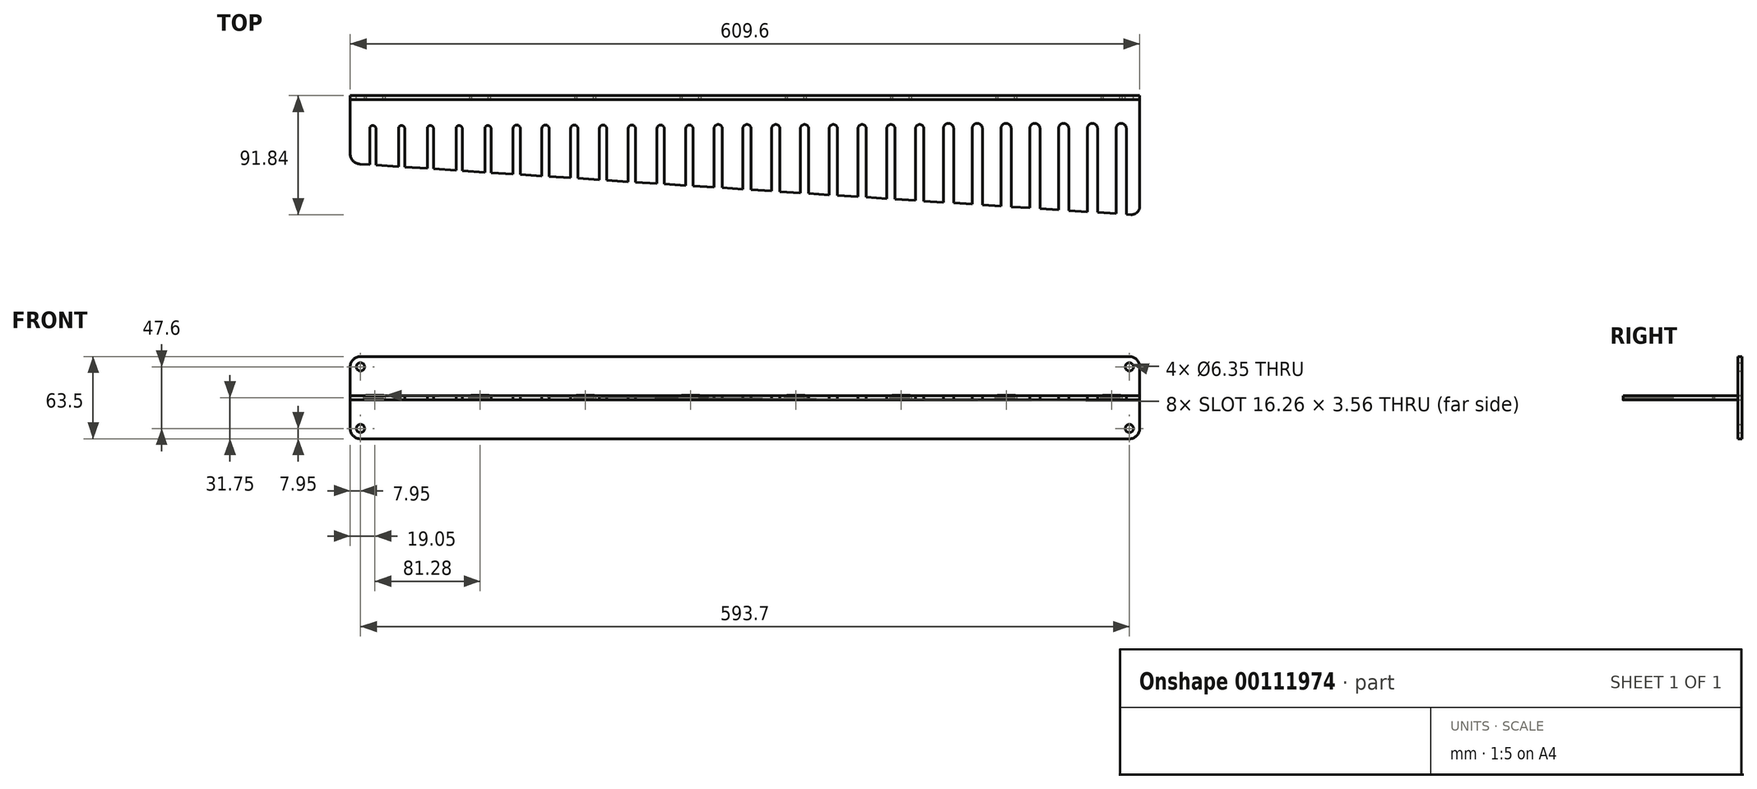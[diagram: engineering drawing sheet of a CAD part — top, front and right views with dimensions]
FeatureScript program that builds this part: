
annotation { "Feature Type Name" : "Feature", "Feature Type Description" : "" }
export const myFeature = defineFeature(function(context is Context, id is Id, definition is map)
    precondition{}
    {
        {
            var Q0;
            Q0=qCreatedBy(makeId("Front.planeOp"),FACE);
            var sketch = newSketch(context, id + "F0", { "sketchPlane" : qUnion([Q0])});
            skLineSegment(sketch, "E0.bottom", {"start": v(-296.85, -31.75) * mm, "end": v(296.85, -31.75) * mm});
            skLineSegment(sketch, "E0.top", {"start": v(-296.85, 31.75) * mm, "end": v(296.85, 31.75) * mm});
            skLineSegment(sketch, "E0.left", {"start": v(-304.8, -23.8) * mm, "end": v(-304.8, 23.8) * mm});
            skLineSegment(sketch, "E0.right", {"start": v(304.8, -23.8) * mm, "end": v(304.8, 23.8) * mm});
            skPoint(sketch, "E0.middle", {"position": v(0, 0) * mm});
            skPoint(sketch, "E1.visualSharp", {"position": v(304.8, 31.75) * mm});
            skArc(sketch, "E1.filletArc", {"start": v(304.8, 23.8) * mm, "mid": v(302.47, 29.42) * mm, "end": v(296.85, 31.75) * mm});
            skPoint(sketch, "E2.visualSharp", {"position": v(304.8, -31.75) * mm});
            skArc(sketch, "E2.filletArc", {"start": v(296.85, -31.75) * mm, "mid": v(302.47, -29.42) * mm, "end": v(304.8, -23.8) * mm});
            skPoint(sketch, "E3.visualSharp", {"position": v(-304.8, -31.75) * mm});
            skArc(sketch, "E3.filletArc", {"start": v(-304.8, -23.8) * mm, "mid": v(-302.47, -29.42) * mm, "end": v(-296.85, -31.75) * mm});
            skPoint(sketch, "E4.visualSharp", {"position": v(-304.8, 31.75) * mm});
            skArc(sketch, "E4.filletArc", {"start": v(-296.85, 31.75) * mm, "mid": v(-302.47, 29.42) * mm, "end": v(-304.8, 23.8) * mm});
            skPoint(sketch, "E5", {"position": v(-304.8, 0) * mm});
            skLineSegment(sketch, "E6", {"start": v(-292.1, 0) * mm, "end": v(-279.4, 0) * mm});
            skArc(sketch, "E7.0.startCap", {"start": v(-292.1, -1.78) * mm, "mid": v(-293.88, 0) * mm, "end": v(-292.1, 1.78) * mm});
            skArc(sketch, "E7.0.endCap", {"start": v(-279.4, 1.78) * mm, "mid": v(-277.62, 0) * mm, "end": v(-279.4, -1.78) * mm});
            skLineSegment(sketch, "E7.0.left", {"start": v(-292.1, 1.78) * mm, "end": v(-279.4, 1.78) * mm});
            skLineSegment(sketch, "E7.0.right", {"start": v(-292.1, -1.78) * mm, "end": v(-279.4, -1.78) * mm});
            skLineSegment(sketch, "E8.1.0.0", {"start": v(-210.82, -1.78) * mm, "end": v(-198.12, -1.78) * mm});
            skLineSegment(sketch, "E8.1.0.1", {"start": v(-210.82, 1.78) * mm, "end": v(-198.12, 1.78) * mm});
            skArc(sketch, "E8.1.0.2", {"start": v(-198.12, 1.78) * mm, "mid": v(-196.34, 0) * mm, "end": v(-198.12, -1.78) * mm});
            skArc(sketch, "E8.1.0.3", {"start": v(-210.82, -1.78) * mm, "mid": v(-212.6, 0) * mm, "end": v(-210.82, 1.78) * mm});
            skLineSegment(sketch, "E8.1.0.4", {"start": v(-210.82, 0) * mm, "end": v(-198.12, 0) * mm});
            skLineSegment(sketch, "E8.2.0.0", {"start": v(-129.54, -1.78) * mm, "end": v(-116.84, -1.78) * mm});
            skLineSegment(sketch, "E8.2.0.1", {"start": v(-129.54, 1.78) * mm, "end": v(-116.84, 1.78) * mm});
            skArc(sketch, "E8.2.0.2", {"start": v(-116.84, 1.78) * mm, "mid": v(-115.06, 0) * mm, "end": v(-116.84, -1.78) * mm});
            skArc(sketch, "E8.2.0.3", {"start": v(-129.54, -1.78) * mm, "mid": v(-131.32, 0) * mm, "end": v(-129.54, 1.78) * mm});
            skLineSegment(sketch, "E8.2.0.4", {"start": v(-129.54, 0) * mm, "end": v(-116.84, 0) * mm});
            skLineSegment(sketch, "E8.3.0.0", {"start": v(-48.26, -1.78) * mm, "end": v(-35.56, -1.78) * mm});
            skLineSegment(sketch, "E8.3.0.1", {"start": v(-48.26, 1.78) * mm, "end": v(-35.56, 1.78) * mm});
            skArc(sketch, "E8.3.0.2", {"start": v(-35.56, 1.78) * mm, "mid": v(-33.78, 0) * mm, "end": v(-35.56, -1.78) * mm});
            skArc(sketch, "E8.3.0.3", {"start": v(-48.26, -1.78) * mm, "mid": v(-50.04, 0) * mm, "end": v(-48.26, 1.78) * mm});
            skLineSegment(sketch, "E8.3.0.4", {"start": v(-48.26, 0) * mm, "end": v(-35.56, 0) * mm});
            skLineSegment(sketch, "E8.4.0.0", {"start": v(33.02, -1.78) * mm, "end": v(45.72, -1.78) * mm});
            skLineSegment(sketch, "E8.4.0.1", {"start": v(33.02, 1.78) * mm, "end": v(45.72, 1.78) * mm});
            skArc(sketch, "E8.4.0.2", {"start": v(45.72, 1.78) * mm, "mid": v(47.5, 0) * mm, "end": v(45.72, -1.78) * mm});
            skArc(sketch, "E8.4.0.3", {"start": v(33.02, -1.78) * mm, "mid": v(31.24, 0) * mm, "end": v(33.02, 1.78) * mm});
            skLineSegment(sketch, "E8.4.0.4", {"start": v(33.02, 0) * mm, "end": v(45.72, 0) * mm});
            skLineSegment(sketch, "E8.5.0.0", {"start": v(114.3, -1.78) * mm, "end": v(127, -1.78) * mm});
            skLineSegment(sketch, "E8.5.0.1", {"start": v(114.3, 1.78) * mm, "end": v(127, 1.78) * mm});
            skArc(sketch, "E8.5.0.2", {"start": v(127, 1.78) * mm, "mid": v(128.78, 0) * mm, "end": v(127, -1.78) * mm});
            skArc(sketch, "E8.5.0.3", {"start": v(114.3, -1.78) * mm, "mid": v(112.52, 0) * mm, "end": v(114.3, 1.78) * mm});
            skLineSegment(sketch, "E8.5.0.4", {"start": v(114.3, 0) * mm, "end": v(127, 0) * mm});
            skLineSegment(sketch, "E8.6.0.0", {"start": v(195.58, -1.78) * mm, "end": v(208.28, -1.78) * mm});
            skLineSegment(sketch, "E8.6.0.1", {"start": v(195.58, 1.78) * mm, "end": v(208.28, 1.78) * mm});
            skArc(sketch, "E8.6.0.2", {"start": v(208.28, 1.78) * mm, "mid": v(210.06, 0) * mm, "end": v(208.28, -1.78) * mm});
            skArc(sketch, "E8.6.0.3", {"start": v(195.58, -1.78) * mm, "mid": v(193.8, 0) * mm, "end": v(195.58, 1.78) * mm});
            skLineSegment(sketch, "E8.6.0.4", {"start": v(195.58, 0) * mm, "end": v(208.28, 0) * mm});
            skLineSegment(sketch, "E8.7.0.0", {"start": v(276.86, -1.78) * mm, "end": v(289.56, -1.78) * mm});
            skLineSegment(sketch, "E8.7.0.1", {"start": v(276.86, 1.78) * mm, "end": v(289.56, 1.78) * mm});
            skArc(sketch, "E8.7.0.2", {"start": v(289.56, 1.78) * mm, "mid": v(291.34, 0) * mm, "end": v(289.56, -1.78) * mm});
            skArc(sketch, "E8.7.0.3", {"start": v(276.86, -1.78) * mm, "mid": v(275.08, 0) * mm, "end": v(276.86, 1.78) * mm});
            skLineSegment(sketch, "E8.7.0.4", {"start": v(276.86, 0) * mm, "end": v(289.56, 0) * mm});
            skLineSegment(sketch, "E8.direction1", {"start": v(-292.1, -1.78) * mm, "end": v(-210.82, -1.78) * mm, "construction": true});
            skCircle(sketch, "E9", {"center": v(-296.85, 23.8) * mm, "radius": 3.18 * mm});
            skCircle(sketch, "E10", {"center": v(-296.85, -23.8) * mm, "radius": 3.18 * mm});
            skCircle(sketch, "E11", {"center": v(296.85, -23.8) * mm, "radius": 3.18 * mm});
            skCircle(sketch, "E12", {"center": v(296.85, 23.8) * mm, "radius": 3.18 * mm});
            skSolve(sketch);
        }
        {
            var Q0;
            Q0 = qSketchRegion(id + "F0", true);
            extrude(context, id + "F1", {"entities" : qUnion([Q0]), "offsetDistance" : 25.4 * mm, "depth" : 3.17 * mm});
        }
        {
            var Q0;
            Q0=makeQuery(id+"F1.opExtrude","SWEPT_FACE",FACE,{"disambiguationData":[OSD([sQuery(id+"F0.wireOp",EDGE,"E7.0.right")])]});
            var sketch = newSketch(context, id + "F2", { "sketchPlane" : qUnion([Q0])});
            skLineSegment(sketch, "E13", {"start": v(289.56, -3.18) * mm, "end": v(304.8, -3.18) * mm});
            skLineSegment(sketch, "E14", {"start": v(208.28, -3.18) * mm, "end": v(276.86, -3.18) * mm});
            skLineSegment(sketch, "E15", {"start": v(127, -3.18) * mm, "end": v(195.58, -3.18) * mm});
            skLineSegment(sketch, "E16", {"start": v(45.72, -3.18) * mm, "end": v(114.3, -3.18) * mm});
            skLineSegment(sketch, "E17", {"start": v(-35.56, -3.18) * mm, "end": v(33.02, -3.18) * mm});
            skLineSegment(sketch, "E18", {"start": v(-116.84, -3.18) * mm, "end": v(-48.26, -3.18) * mm});
            skLineSegment(sketch, "E19", {"start": v(-198.12, -3.18) * mm, "end": v(-129.54, -3.18) * mm});
            skLineSegment(sketch, "E20", {"start": v(-279.4, -3.18) * mm, "end": v(-210.82, -3.18) * mm});
            skLineSegment(sketch, "E21", {"start": v(-304.8, -3.18) * mm, "end": v(-292.1, -3.18) * mm});
            skLineSegment(sketch, "E22", {"start": v(-292.1, 0) * mm, "end": v(-279.4, 0) * mm});
            skLineSegment(sketch, "E23", {"start": v(-292.1, -3.18) * mm, "end": v(-292.1, 0) * mm});
            skLineSegment(sketch, "E24", {"start": v(-279.4, -3.18) * mm, "end": v(-279.4, 0) * mm});
            skLineSegment(sketch, "E25", {"start": v(-210.82, 0) * mm, "end": v(-198.12, 0) * mm});
            skLineSegment(sketch, "E26", {"start": v(-210.82, -3.18) * mm, "end": v(-210.82, 0) * mm});
            skLineSegment(sketch, "E27", {"start": v(-198.12, -3.18) * mm, "end": v(-198.12, 0) * mm});
            skLineSegment(sketch, "E28", {"start": v(-129.54, 0) * mm, "end": v(-116.84, 0) * mm});
            skLineSegment(sketch, "E29", {"start": v(-129.54, -3.18) * mm, "end": v(-129.54, 0) * mm});
            skLineSegment(sketch, "E30", {"start": v(-116.84, -3.18) * mm, "end": v(-116.84, 0) * mm});
            skLineSegment(sketch, "E31", {"start": v(-48.26, 0) * mm, "end": v(-35.56, 0) * mm});
            skLineSegment(sketch, "E32", {"start": v(-48.26, -3.18) * mm, "end": v(-48.26, 0) * mm});
            skLineSegment(sketch, "E33", {"start": v(-35.56, -3.18) * mm, "end": v(-35.56, 0) * mm});
            skLineSegment(sketch, "E34", {"start": v(33.02, 0) * mm, "end": v(45.72, 0) * mm});
            skLineSegment(sketch, "E35", {"start": v(33.02, -3.18) * mm, "end": v(33.02, 0) * mm});
            skLineSegment(sketch, "E36", {"start": v(45.72, -3.18) * mm, "end": v(45.72, 0) * mm});
            skLineSegment(sketch, "E37", {"start": v(114.3, 0) * mm, "end": v(127, 0) * mm});
            skLineSegment(sketch, "E38", {"start": v(114.3, -3.18) * mm, "end": v(114.3, 0) * mm});
            skLineSegment(sketch, "E39", {"start": v(127, -3.18) * mm, "end": v(127, 0) * mm});
            skLineSegment(sketch, "E40", {"start": v(195.58, 0) * mm, "end": v(208.28, 0) * mm});
            skLineSegment(sketch, "E41", {"start": v(195.58, -3.18) * mm, "end": v(195.58, 0) * mm});
            skLineSegment(sketch, "E42", {"start": v(208.28, -3.18) * mm, "end": v(208.28, 0) * mm});
            skLineSegment(sketch, "E43", {"start": v(276.86, 0) * mm, "end": v(289.56, 0) * mm});
            skLineSegment(sketch, "E44", {"start": v(276.86, -3.18) * mm, "end": v(276.86, 0) * mm});
            skLineSegment(sketch, "E45", {"start": v(289.56, -3.18) * mm, "end": v(289.56, 0) * mm});
            skPoint(sketch, "E46.end.orphan", {"position": v(-279.4, -3.18) * mm});
            skPoint(sketch, "E46.start.orphan", {"position": v(-292.1, -3.18) * mm});
            skPoint(sketch, "E47.end.orphan", {"position": v(-198.12, -3.18) * mm});
            skPoint(sketch, "E47.start.orphan", {"position": v(-210.82, -3.18) * mm});
            skPoint(sketch, "E48.end.orphan", {"position": v(-116.84, -3.18) * mm});
            skPoint(sketch, "E48.start.orphan", {"position": v(-129.54, -3.18) * mm});
            skPoint(sketch, "E49.end.orphan", {"position": v(45.72, -3.18) * mm});
            skPoint(sketch, "E49.start.orphan", {"position": v(33.02, -3.18) * mm});
            skPoint(sketch, "E50.end.orphan", {"position": v(127, -3.18) * mm});
            skPoint(sketch, "E50.start.orphan", {"position": v(114.3, -3.18) * mm});
            skPoint(sketch, "E51.end.orphan", {"position": v(-35.56, -3.18) * mm});
            skPoint(sketch, "E51.start.orphan", {"position": v(-48.26, -3.18) * mm});
            skPoint(sketch, "E52.end.orphan", {"position": v(208.28, -3.18) * mm});
            skPoint(sketch, "E52.start.orphan", {"position": v(195.58, -3.18) * mm});
            skPoint(sketch, "E53.end.orphan", {"position": v(289.56, -3.18) * mm});
            skPoint(sketch, "E53.start.orphan", {"position": v(276.86, -3.18) * mm});
            skLineSegment(sketch, "E54", {"start": v(-297.37, -52.8) * mm, "end": v(298.03, -91.82) * mm});
            skLineSegment(sketch, "E55", {"start": v(304.8, -85.49) * mm, "end": v(304.8, -3.17) * mm});
            skPoint(sketch, "E56.visualSharp", {"position": v(304.8, -92.27) * mm});
            skArc(sketch, "E56.filletArc", {"start": v(298.03, -91.82) * mm, "mid": v(302.8, -90.12) * mm, "end": v(304.8, -85.49) * mm});
            skLineSegment(sketch, "E57", {"start": v(-304.8, -3.18) * mm, "end": v(-304.8, -44.87) * mm});
            skPoint(sketch, "E58.visualSharp", {"position": v(-304.8, -52.31) * mm});
            skArc(sketch, "E58.filletArc", {"start": v(-304.8, -44.87) * mm, "mid": v(-302.65, -50.3) * mm, "end": v(-297.37, -52.8) * mm});
            skLineSegment(sketch, "E59", {"start": v(290.51, -91.33) * mm, "end": v(290.51, -25.4) * mm});
            skLineSegment(sketch, "E60.1.0.0", {"start": v(268.29, -91.33) * mm, "end": v(268.29, -25.4) * mm});
            skLineSegment(sketch, "E60.2.0.0", {"start": v(246.06, -91.33) * mm, "end": v(246.06, -25.4) * mm});
            skLineSegment(sketch, "E60.direction1", {"start": v(290.51, -91.33) * mm, "end": v(268.29, -91.33) * mm, "construction": true});
            skLineSegment(sketch, "E61.0.3.0", {"start": v(223.84, -91.33) * mm, "end": v(223.84, -25.4) * mm});
            skLineSegment(sketch, "E61.0.4.0", {"start": v(201.61, -91.33) * mm, "end": v(201.61, -25.4) * mm});
            skLineSegment(sketch, "E61.0.5.0", {"start": v(179.39, -91.33) * mm, "end": v(179.39, -25.4) * mm});
            skLineSegment(sketch, "E62.0.6.0", {"start": v(157.16, -91.33) * mm, "end": v(157.16, -25.4) * mm});
            skLineSegment(sketch, "E63.0.7.0", {"start": v(134.94, -91.33) * mm, "end": v(134.94, -25.4) * mm});
            skLineSegment(sketch, "E64.0.8.0", {"start": v(112.71, -91.33) * mm, "end": v(112.71, -25.4) * mm});
            skLineSegment(sketch, "E65.0.9.0", {"start": v(90.49, -91.33) * mm, "end": v(90.49, -25.4) * mm});
            skLineSegment(sketch, "E66.0.10.0", {"start": v(68.26, -91.33) * mm, "end": v(68.26, -25.4) * mm});
            skLineSegment(sketch, "E67.0.11.0", {"start": v(46.04, -91.33) * mm, "end": v(46.04, -25.4) * mm});
            skLineSegment(sketch, "E68.0.12.0", {"start": v(23.81, -91.33) * mm, "end": v(23.81, -25.4) * mm});
            skLineSegment(sketch, "E69.0.13.0", {"start": v(1.59, -91.33) * mm, "end": v(1.59, -25.4) * mm});
            skLineSegment(sketch, "E70.0.14.0", {"start": v(-20.64, -91.33) * mm, "end": v(-20.64, -25.4) * mm});
            skLineSegment(sketch, "E71.0.15.0", {"start": v(-42.86, -91.33) * mm, "end": v(-42.86, -25.4) * mm});
            skLineSegment(sketch, "E72.0.16.0", {"start": v(-65.09, -91.33) * mm, "end": v(-65.09, -25.4) * mm});
            skLineSegment(sketch, "E73.0.17.0", {"start": v(-87.31, -91.33) * mm, "end": v(-87.31, -25.4) * mm});
            skLineSegment(sketch, "E74.0.18.0", {"start": v(-109.54, -91.33) * mm, "end": v(-109.54, -25.4) * mm});
            skLineSegment(sketch, "E75.0.19.0", {"start": v(-131.76, -91.33) * mm, "end": v(-131.76, -25.4) * mm});
            skLineSegment(sketch, "E76.0.20.0", {"start": v(-153.99, -91.33) * mm, "end": v(-153.99, -25.4) * mm});
            skLineSegment(sketch, "E77.0.21.0", {"start": v(-176.21, -91.33) * mm, "end": v(-176.21, -25.4) * mm});
            skLineSegment(sketch, "E78.0.22.0", {"start": v(-198.44, -91.33) * mm, "end": v(-198.44, -25.4) * mm});
            skLineSegment(sketch, "E79.0.23.0", {"start": v(-220.66, -91.33) * mm, "end": v(-220.66, -25.4) * mm});
            skLineSegment(sketch, "E80.0.24.0", {"start": v(-242.89, -91.33) * mm, "end": v(-242.89, -25.4) * mm});
            skLineSegment(sketch, "E81.0.25.0", {"start": v(-265.11, -91.33) * mm, "end": v(-265.11, -25.4) * mm});
            skLineSegment(sketch, "E82.0.26.0", {"start": v(-287.34, -91.33) * mm, "end": v(-287.34, -25.4) * mm});
            skArc(sketch, "E83.0.startCap", {"start": v(294.49, -91.33) * mm, "mid": v(290.51, -95.3) * mm, "end": v(286.54, -91.33) * mm});
            skArc(sketch, "E83.0.endCap", {"start": v(286.54, -25.4) * mm, "mid": v(290.51, -21.42) * mm, "end": v(294.49, -25.4) * mm});
            skLineSegment(sketch, "E83.0.left", {"start": v(286.54, -91.33) * mm, "end": v(286.54, -25.4) * mm});
            skLineSegment(sketch, "E83.0.right", {"start": v(294.49, -91.33) * mm, "end": v(294.49, -25.4) * mm});
            skArc(sketch, "E83.1.startCap", {"start": v(272.26, -91.33) * mm, "mid": v(268.29, -95.3) * mm, "end": v(264.31, -91.33) * mm});
            skArc(sketch, "E83.1.endCap", {"start": v(264.31, -25.4) * mm, "mid": v(268.29, -21.42) * mm, "end": v(272.26, -25.4) * mm});
            skLineSegment(sketch, "E83.1.left", {"start": v(264.31, -91.33) * mm, "end": v(264.31, -25.4) * mm});
            skLineSegment(sketch, "E83.1.right", {"start": v(272.26, -91.33) * mm, "end": v(272.26, -25.4) * mm});
            skArc(sketch, "E83.2.startCap", {"start": v(250.04, -91.33) * mm, "mid": v(246.06, -95.3) * mm, "end": v(242.09, -91.33) * mm});
            skArc(sketch, "E83.2.endCap", {"start": v(242.09, -25.4) * mm, "mid": v(246.06, -21.42) * mm, "end": v(250.04, -25.4) * mm});
            skLineSegment(sketch, "E83.2.left", {"start": v(242.09, -91.33) * mm, "end": v(242.09, -25.4) * mm});
            skLineSegment(sketch, "E83.2.right", {"start": v(250.04, -91.33) * mm, "end": v(250.04, -25.4) * mm});
            skArc(sketch, "E83.3.startCap", {"start": v(227.81, -91.33) * mm, "mid": v(223.84, -95.3) * mm, "end": v(219.86, -91.33) * mm});
            skArc(sketch, "E83.3.endCap", {"start": v(219.86, -25.4) * mm, "mid": v(223.84, -21.42) * mm, "end": v(227.81, -25.4) * mm});
            skLineSegment(sketch, "E83.3.left", {"start": v(219.86, -91.33) * mm, "end": v(219.86, -25.4) * mm});
            skLineSegment(sketch, "E83.3.right", {"start": v(227.81, -91.33) * mm, "end": v(227.81, -25.4) * mm});
            skArc(sketch, "E83.4.startCap", {"start": v(205.59, -91.33) * mm, "mid": v(201.61, -95.3) * mm, "end": v(197.64, -91.33) * mm});
            skArc(sketch, "E83.4.endCap", {"start": v(197.64, -25.4) * mm, "mid": v(201.61, -21.42) * mm, "end": v(205.59, -25.4) * mm});
            skLineSegment(sketch, "E83.4.left", {"start": v(197.64, -91.33) * mm, "end": v(197.64, -25.4) * mm});
            skLineSegment(sketch, "E83.4.right", {"start": v(205.59, -91.33) * mm, "end": v(205.59, -25.4) * mm});
            skArc(sketch, "E83.5.startCap", {"start": v(183.36, -91.33) * mm, "mid": v(179.39, -95.3) * mm, "end": v(175.41, -91.33) * mm});
            skArc(sketch, "E83.5.endCap", {"start": v(175.41, -25.4) * mm, "mid": v(179.39, -21.42) * mm, "end": v(183.36, -25.4) * mm});
            skLineSegment(sketch, "E83.5.left", {"start": v(175.41, -91.33) * mm, "end": v(175.41, -25.4) * mm});
            skLineSegment(sketch, "E83.5.right", {"start": v(183.36, -91.33) * mm, "end": v(183.36, -25.4) * mm});
            skArc(sketch, "E83.6.startCap", {"start": v(161.14, -91.33) * mm, "mid": v(157.16, -95.3) * mm, "end": v(153.19, -91.33) * mm});
            skArc(sketch, "E83.6.endCap", {"start": v(153.19, -25.4) * mm, "mid": v(157.16, -21.42) * mm, "end": v(161.14, -25.4) * mm});
            skLineSegment(sketch, "E83.6.left", {"start": v(153.19, -91.33) * mm, "end": v(153.19, -25.4) * mm});
            skLineSegment(sketch, "E83.6.right", {"start": v(161.14, -91.33) * mm, "end": v(161.14, -25.4) * mm});
            skArc(sketch, "E84.0.startCap", {"start": v(-284.96, -91.33) * mm, "mid": v(-287.34, -93.7) * mm, "end": v(-289.71, -91.33) * mm});
            skArc(sketch, "E84.0.endCap", {"start": v(-289.71, -25.4) * mm, "mid": v(-287.34, -23.03) * mm, "end": v(-284.96, -25.4) * mm});
            skLineSegment(sketch, "E84.0.left", {"start": v(-289.71, -91.33) * mm, "end": v(-289.71, -25.4) * mm});
            skLineSegment(sketch, "E84.0.right", {"start": v(-284.96, -91.33) * mm, "end": v(-284.96, -25.4) * mm});
            skArc(sketch, "E84.1.startCap", {"start": v(-262.74, -91.33) * mm, "mid": v(-265.11, -93.7) * mm, "end": v(-267.49, -91.33) * mm});
            skArc(sketch, "E84.1.endCap", {"start": v(-267.49, -25.4) * mm, "mid": v(-265.11, -23.03) * mm, "end": v(-262.74, -25.4) * mm});
            skLineSegment(sketch, "E84.1.left", {"start": v(-267.49, -91.33) * mm, "end": v(-267.49, -25.4) * mm});
            skLineSegment(sketch, "E84.1.right", {"start": v(-262.74, -91.33) * mm, "end": v(-262.74, -25.4) * mm});
            skArc(sketch, "E84.2.startCap", {"start": v(-240.51, -91.33) * mm, "mid": v(-242.89, -93.7) * mm, "end": v(-245.26, -91.33) * mm});
            skArc(sketch, "E84.2.endCap", {"start": v(-245.26, -25.4) * mm, "mid": v(-242.89, -23.03) * mm, "end": v(-240.51, -25.4) * mm});
            skLineSegment(sketch, "E84.2.left", {"start": v(-245.26, -91.33) * mm, "end": v(-245.26, -25.4) * mm});
            skLineSegment(sketch, "E84.2.right", {"start": v(-240.51, -91.33) * mm, "end": v(-240.51, -25.4) * mm});
            skArc(sketch, "E84.3.startCap", {"start": v(-218.29, -91.33) * mm, "mid": v(-220.66, -93.7) * mm, "end": v(-223.04, -91.33) * mm});
            skArc(sketch, "E84.3.endCap", {"start": v(-223.04, -25.4) * mm, "mid": v(-220.66, -23.03) * mm, "end": v(-218.29, -25.4) * mm});
            skLineSegment(sketch, "E84.3.left", {"start": v(-223.04, -91.33) * mm, "end": v(-223.04, -25.4) * mm});
            skLineSegment(sketch, "E84.3.right", {"start": v(-218.29, -91.33) * mm, "end": v(-218.29, -25.4) * mm});
            skArc(sketch, "E84.4.startCap", {"start": v(-196.06, -91.33) * mm, "mid": v(-198.44, -93.7) * mm, "end": v(-200.81, -91.33) * mm});
            skArc(sketch, "E84.4.endCap", {"start": v(-200.81, -25.4) * mm, "mid": v(-198.44, -23.03) * mm, "end": v(-196.06, -25.4) * mm});
            skLineSegment(sketch, "E84.4.left", {"start": v(-200.81, -91.33) * mm, "end": v(-200.81, -25.4) * mm});
            skLineSegment(sketch, "E84.4.right", {"start": v(-196.06, -91.33) * mm, "end": v(-196.06, -25.4) * mm});
            skArc(sketch, "E85.0.startCap", {"start": v(-173.43, -91.33) * mm, "mid": v(-176.21, -94.1) * mm, "end": v(-179, -91.33) * mm});
            skArc(sketch, "E85.0.endCap", {"start": v(-179, -25.4) * mm, "mid": v(-176.21, -22.62) * mm, "end": v(-173.43, -25.4) * mm});
            skLineSegment(sketch, "E85.0.left", {"start": v(-179, -91.33) * mm, "end": v(-179, -25.4) * mm});
            skLineSegment(sketch, "E85.0.right", {"start": v(-173.43, -91.33) * mm, "end": v(-173.43, -25.4) * mm});
            skArc(sketch, "E85.1.startCap", {"start": v(-151.2, -91.33) * mm, "mid": v(-153.99, -94.1) * mm, "end": v(-156.77, -91.33) * mm});
            skArc(sketch, "E85.1.endCap", {"start": v(-156.77, -25.4) * mm, "mid": v(-153.99, -22.62) * mm, "end": v(-151.2, -25.4) * mm});
            skLineSegment(sketch, "E85.1.left", {"start": v(-156.77, -91.33) * mm, "end": v(-156.77, -25.4) * mm});
            skLineSegment(sketch, "E85.1.right", {"start": v(-151.2, -91.33) * mm, "end": v(-151.2, -25.4) * mm});
            skArc(sketch, "E85.2.startCap", {"start": v(-128.98, -91.33) * mm, "mid": v(-131.76, -94.1) * mm, "end": v(-134.54, -91.33) * mm});
            skArc(sketch, "E85.2.endCap", {"start": v(-134.54, -25.4) * mm, "mid": v(-131.76, -22.62) * mm, "end": v(-128.98, -25.4) * mm});
            skLineSegment(sketch, "E85.2.left", {"start": v(-134.54, -91.33) * mm, "end": v(-134.54, -25.4) * mm});
            skLineSegment(sketch, "E85.2.right", {"start": v(-128.98, -91.33) * mm, "end": v(-128.98, -25.4) * mm});
            skArc(sketch, "E85.3.startCap", {"start": v(-106.76, -91.33) * mm, "mid": v(-109.54, -94.1) * mm, "end": v(-112.32, -91.33) * mm});
            skArc(sketch, "E85.3.endCap", {"start": v(-112.32, -25.4) * mm, "mid": v(-109.54, -22.62) * mm, "end": v(-106.76, -25.4) * mm});
            skLineSegment(sketch, "E85.3.left", {"start": v(-112.32, -91.33) * mm, "end": v(-112.32, -25.4) * mm});
            skLineSegment(sketch, "E85.3.right", {"start": v(-106.76, -91.33) * mm, "end": v(-106.76, -25.4) * mm});
            skArc(sketch, "E85.4.startCap", {"start": v(-84.53, -91.33) * mm, "mid": v(-87.31, -94.1) * mm, "end": v(-90.1, -91.33) * mm});
            skArc(sketch, "E85.4.endCap", {"start": v(-90.1, -25.4) * mm, "mid": v(-87.31, -22.62) * mm, "end": v(-84.53, -25.4) * mm});
            skLineSegment(sketch, "E85.4.left", {"start": v(-90.1, -91.33) * mm, "end": v(-90.1, -25.4) * mm});
            skLineSegment(sketch, "E85.4.right", {"start": v(-84.53, -91.33) * mm, "end": v(-84.53, -25.4) * mm});
            skArc(sketch, "E85.5.startCap", {"start": v(-62.3, -91.33) * mm, "mid": v(-65.09, -94.1) * mm, "end": v(-67.87, -91.33) * mm});
            skArc(sketch, "E85.5.endCap", {"start": v(-67.87, -25.4) * mm, "mid": v(-65.09, -22.62) * mm, "end": v(-62.3, -25.4) * mm});
            skLineSegment(sketch, "E85.5.left", {"start": v(-67.87, -91.33) * mm, "end": v(-67.87, -25.4) * mm});
            skLineSegment(sketch, "E85.5.right", {"start": v(-62.3, -91.33) * mm, "end": v(-62.3, -25.4) * mm});
            skArc(sketch, "E85.6.startCap", {"start": v(-40.08, -91.33) * mm, "mid": v(-42.86, -94.1) * mm, "end": v(-45.64, -91.33) * mm});
            skArc(sketch, "E85.6.endCap", {"start": v(-45.64, -25.4) * mm, "mid": v(-42.86, -22.62) * mm, "end": v(-40.08, -25.4) * mm});
            skLineSegment(sketch, "E85.6.left", {"start": v(-45.64, -91.33) * mm, "end": v(-45.64, -25.4) * mm});
            skLineSegment(sketch, "E85.6.right", {"start": v(-40.08, -91.33) * mm, "end": v(-40.08, -25.4) * mm});
            skArc(sketch, "E86.0.startCap", {"start": v(-17.46, -91.33) * mm, "mid": v(-20.64, -94.5) * mm, "end": v(-23.81, -91.33) * mm});
            skArc(sketch, "E86.0.endCap", {"start": v(-23.81, -25.4) * mm, "mid": v(-20.64, -22.23) * mm, "end": v(-17.46, -25.4) * mm});
            skLineSegment(sketch, "E86.0.left", {"start": v(-23.81, -91.33) * mm, "end": v(-23.81, -25.4) * mm});
            skLineSegment(sketch, "E86.0.right", {"start": v(-17.46, -91.33) * mm, "end": v(-17.46, -25.4) * mm});
            skArc(sketch, "E86.1.startCap", {"start": v(4.76, -91.33) * mm, "mid": v(1.59, -94.5) * mm, "end": v(-1.59, -91.33) * mm});
            skArc(sketch, "E86.1.endCap", {"start": v(-1.59, -25.4) * mm, "mid": v(1.59, -22.23) * mm, "end": v(4.76, -25.4) * mm});
            skLineSegment(sketch, "E86.1.left", {"start": v(-1.59, -91.33) * mm, "end": v(-1.59, -25.4) * mm});
            skLineSegment(sketch, "E86.1.right", {"start": v(4.76, -91.33) * mm, "end": v(4.76, -25.4) * mm});
            skArc(sketch, "E86.2.startCap", {"start": v(26.99, -91.33) * mm, "mid": v(23.81, -94.5) * mm, "end": v(20.64, -91.33) * mm});
            skArc(sketch, "E86.2.endCap", {"start": v(20.64, -25.4) * mm, "mid": v(23.81, -22.23) * mm, "end": v(26.99, -25.4) * mm});
            skLineSegment(sketch, "E86.2.left", {"start": v(20.64, -91.33) * mm, "end": v(20.64, -25.4) * mm});
            skLineSegment(sketch, "E86.2.right", {"start": v(26.99, -91.33) * mm, "end": v(26.99, -25.4) * mm});
            skArc(sketch, "E86.3.startCap", {"start": v(49.21, -91.33) * mm, "mid": v(46.04, -94.5) * mm, "end": v(42.86, -91.33) * mm});
            skArc(sketch, "E86.3.endCap", {"start": v(42.86, -25.4) * mm, "mid": v(46.04, -22.23) * mm, "end": v(49.21, -25.4) * mm});
            skLineSegment(sketch, "E86.3.left", {"start": v(42.86, -91.33) * mm, "end": v(42.86, -25.4) * mm});
            skLineSegment(sketch, "E86.3.right", {"start": v(49.21, -91.33) * mm, "end": v(49.21, -25.4) * mm});
            skArc(sketch, "E86.4.startCap", {"start": v(71.44, -91.33) * mm, "mid": v(68.26, -94.5) * mm, "end": v(65.09, -91.33) * mm});
            skArc(sketch, "E86.4.endCap", {"start": v(65.09, -25.4) * mm, "mid": v(68.26, -22.23) * mm, "end": v(71.44, -25.4) * mm});
            skLineSegment(sketch, "E86.4.left", {"start": v(65.09, -91.33) * mm, "end": v(65.09, -25.4) * mm});
            skLineSegment(sketch, "E86.4.right", {"start": v(71.44, -91.33) * mm, "end": v(71.44, -25.4) * mm});
            skArc(sketch, "E86.5.startCap", {"start": v(93.66, -91.33) * mm, "mid": v(90.49, -94.5) * mm, "end": v(87.31, -91.33) * mm});
            skArc(sketch, "E86.5.endCap", {"start": v(87.31, -25.4) * mm, "mid": v(90.49, -22.23) * mm, "end": v(93.66, -25.4) * mm});
            skLineSegment(sketch, "E86.5.left", {"start": v(87.31, -91.33) * mm, "end": v(87.31, -25.4) * mm});
            skLineSegment(sketch, "E86.5.right", {"start": v(93.66, -91.33) * mm, "end": v(93.66, -25.4) * mm});
            skArc(sketch, "E86.6.startCap", {"start": v(115.89, -91.33) * mm, "mid": v(112.71, -94.5) * mm, "end": v(109.54, -91.33) * mm});
            skArc(sketch, "E86.6.endCap", {"start": v(109.54, -25.4) * mm, "mid": v(112.71, -22.23) * mm, "end": v(115.89, -25.4) * mm});
            skLineSegment(sketch, "E86.6.left", {"start": v(109.54, -91.33) * mm, "end": v(109.54, -25.4) * mm});
            skLineSegment(sketch, "E86.6.right", {"start": v(115.89, -91.33) * mm, "end": v(115.89, -25.4) * mm});
            skArc(sketch, "E86.7.startCap", {"start": v(138.11, -91.33) * mm, "mid": v(134.94, -94.5) * mm, "end": v(131.76, -91.33) * mm});
            skArc(sketch, "E86.7.endCap", {"start": v(131.76, -25.4) * mm, "mid": v(134.94, -22.23) * mm, "end": v(138.11, -25.4) * mm});
            skLineSegment(sketch, "E86.7.left", {"start": v(131.76, -91.33) * mm, "end": v(131.76, -25.4) * mm});
            skLineSegment(sketch, "E86.7.right", {"start": v(138.11, -91.33) * mm, "end": v(138.11, -25.4) * mm});
            skSolve(sketch);
        }
        {
            var Q0;
            Q0=makeQuery(id+"F2.imprint","IMPRINT",FACE,{"disambiguationData":[TD([[makeQuery(id+"F2.imprint","IMPRINT",EDGE,{"derivedFrom":sQuery(id+"F2.wireOp",EDGE,"E13")}),-1.0]])]});
            var Q1;
            Q1=makeQuery(id+"F2.imprint","IMPRINT",FACE,{"disambiguationData":[TD([[makeQuery(id+"F2.imprint","IMPRINT",EDGE,{"derivedFrom":sQuery(id+"F2.wireOp",EDGE,"E22")}),-1.0]])]});
            extrude(context, id + "F3", {"entities" : qUnion([Q0, Q1]), "depth" : 3.17 * mm, "offsetDistance" : 25.4 * mm});
        }
    });
